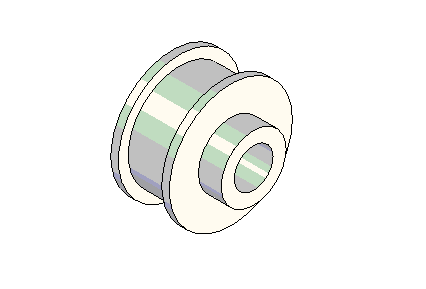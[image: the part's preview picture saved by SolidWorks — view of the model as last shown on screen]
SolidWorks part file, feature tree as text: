
SOLIDWORKS PART (.sldprt)
format: sldprt  version: not decoded by parser v0  size: 141,824 bytes
history: native  units: mm
features: sketch x5, extrude x4, cut_extrude x1 (+11 scaffold rows collapsed)
feature tree (21):
  scaffold x11  (default folders/planes/origin — collapsed)
  sketch  "Sketch1"  dims[D1=15.875mm]
  extrude  "Extrude1"  Depth=5.55625mm
  sketch  "Sketch2"  dims[D1=30.0736mm]
  extrude  "Extrude2"  Depth=1.83515mm
  sketch  "Sketch3"  dims[D1=25.273mm]
  extrude  "Extrude3"  Depth=10.6172mm
  sketch  "Sketch4"
  extrude  "Extrude4"  Depth=1.83515mm
  sketch  "Sketch5"  dims[D1=9.525mm]
  cut_extrude  "Cut-Extrude1"  [1 undecoded]
decode coverage: 8 of 10 modeling features carry decoded parameters
note: 1 parameter value undecoded
note: suppression state not decoded; provenance and decode notes live in map.json
